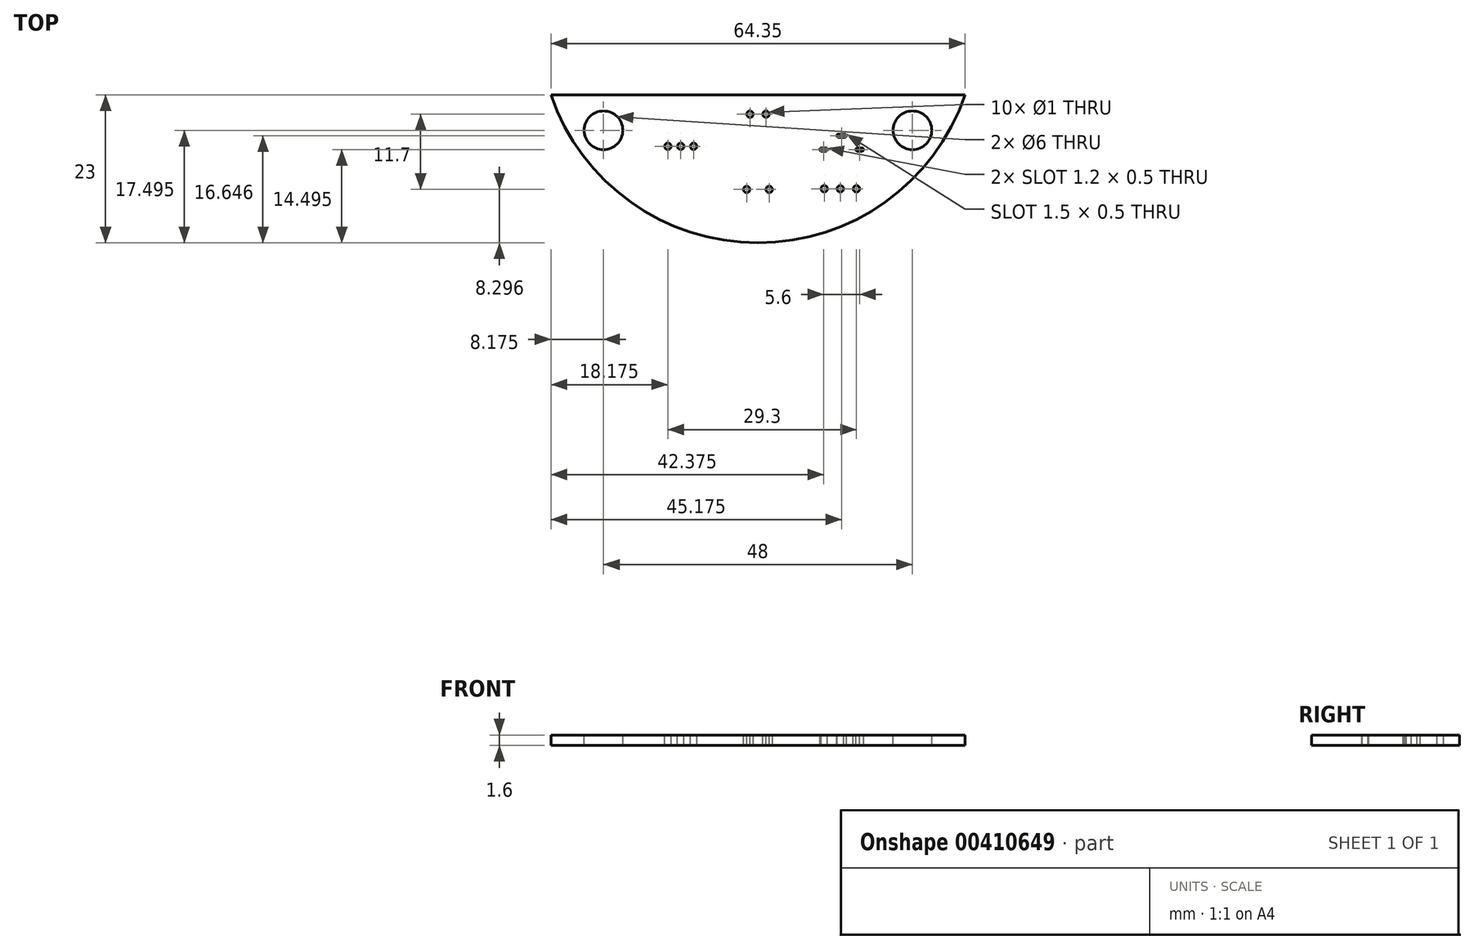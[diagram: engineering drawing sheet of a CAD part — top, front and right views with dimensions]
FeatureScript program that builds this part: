
annotation { "Feature Type Name" : "Feature", "Feature Type Description" : "" }
export const myFeature = defineFeature(function(context is Context, id is Id, definition is map)
    precondition{}
    {
        {
            var Q0;
            Q0=qCreatedBy(makeId("Top.planeOp"),FACE);
            var sketch = newSketch(context, id + "F0", { "sketchPlane" : qUnion([Q0])});
            skLineSegment(sketch, "E0.bottom", {"start": v(6.37, 29.29) * mm, "end": v(70.72, 29.29) * mm});
            skPoint(sketch, "E1.middle", {"position": v(38.54, 20.77) * mm});
            skPoint(sketch, "E2.orphan", {"position": v(18.04, 25.29) * mm});
            skPoint(sketch, "E3.orphan", {"position": v(59.04, 25.29) * mm});
            skArc(sketch, "E4", {"start": v(6.37, 29.29) * mm, "mid": v(38.54, 6.29) * mm, "end": v(70.72, 29.29) * mm});
            skSolve(sketch);
        }
        {
            var Q0;
            Q0=qSketchRegion(id+"F0",true);
            extrude(context, id + "F1", {"entities" : qUnion([Q0]), "depth" : 1.6 * mm});
        }
        {
            var Q0;
            Q0=makeQuery(id+"F1.opExtrude","CAP_FACE",FACE,{"disambiguationData":[OSD([sQuery(id+"F0.wireOp",EDGE,"E0.bottom"),sQuery(id+"F0.wireOp",EDGE,"E0.top"),sQuery(id+"F0.wireOp",EDGE,"E0.left"),sQuery(id+"F0.wireOp",EDGE,"E0.right"),sQuery(id+"F0.wireOp",EDGE,"E1.bottom"),sQuery(id+"F0.wireOp",EDGE,"E1.left"),sQuery(id+"F0.wireOp",EDGE,"E1.right")])],"isStart":false});
            var sketch = newSketch(context, id + "F2", { "sketchPlane" : qUnion([Q0])});
            skCircle(sketch, "E5", {"center": v(14.54, 23.79) * mm, "radius": 3 * mm});
            skLineSegment(sketch, "E6", {"start": v(38.54, 20.12) * mm, "end": v(38.54, 29.29) * mm, "construction": true});
            skCircle(sketch, "E7.MirrorC", {"center": v(62.54, 23.79) * mm, "radius": 3 * mm});
            skSolve(sketch);
        }
        {
            var Q0;
            Q0=qSketchRegion(id+"F2",true);
            extrude(context, id + "F3", {"entities" : qUnion([Q0]), "operationType" : NewBodyOperationType.REMOVE, "oppositeDirection" : true, "depth" : 3 * mm});
        }
        {
            var Q0;
            Q0=makeQuery(id+"F1.opExtrude","CAP_FACE",FACE,{"disambiguationData":[OSD([sQuery(id+"F0.wireOp",EDGE,"E0.bottom"),sQuery(id+"F0.wireOp",EDGE,"E0.top"),sQuery(id+"F0.wireOp",EDGE,"E0.left"),sQuery(id+"F0.wireOp",EDGE,"E0.right"),sQuery(id+"F0.wireOp",EDGE,"E1.bottom"),sQuery(id+"F0.wireOp",EDGE,"E1.left"),sQuery(id+"F0.wireOp",EDGE,"E1.right")])],"isStart":false});
            var sketch = newSketch(context, id + "F4", { "sketchPlane" : qUnion([Q0])});
            skCircle(sketch, "E8", {"center": v(24.54, 21.29) * mm, "radius": 0.5 * mm});
            skLineSegment(sketch, "E9", {"start": v(38.54, 22.32) * mm, "end": v(38.54, 29.29) * mm, "construction": true});
            skCircle(sketch, "E10.1.0.0", {"center": v(26.54, 21.29) * mm, "radius": 0.5 * mm});
            skLineSegment(sketch, "E10.direction1", {"start": v(24.54, 21.29) * mm, "end": v(26.54, 21.29) * mm, "construction": true});
            skCircle(sketch, "E11.0.2.0", {"center": v(28.54, 21.29) * mm, "radius": 0.5 * mm});
            skSolve(sketch);
        }
        {
            var Q0;
            Q0=makeQuery(id+"F1.opExtrude","CAP_FACE",FACE,{"disambiguationData":[OSD([sQuery(id+"F0.wireOp",EDGE,"E0.bottom"),sQuery(id+"F0.wireOp",EDGE,"E4")])],"isStart":false});
            var sketch = newSketch(context, id + "F5", { "sketchPlane" : qUnion([Q0])});
            skLineSegment(sketch, "E12", {"start": v(51.54, 14.1) * mm, "end": v(51.54, 27.42) * mm, "construction": true});
            skLineSegment(sketch, "E13", {"start": v(38.54, 6.29) * mm, "end": v(38.54, 24.04) * mm, "construction": true});
            skLineSegment(sketch, "E14", {"start": v(48.4, 20.79) * mm, "end": v(49.1, 20.79) * mm, "construction": true});
            skLineSegment(sketch, "E15", {"start": v(48.74, 20.79) * mm, "end": v(48.74, 23.97) * mm, "construction": true});
            skLineSegment(sketch, "E16", {"start": v(51.04, 22.94) * mm, "end": v(52.04, 22.94) * mm, "construction": true});
            skLineSegment(sketch, "E17", {"start": v(51.54, 22.94) * mm, "end": v(51.54, 19.92) * mm, "construction": true});
            skArc(sketch, "E18.0.startCap", {"start": v(51.04, 22.69) * mm, "mid": v(50.8, 22.94) * mm, "end": v(51.04, 23.19) * mm});
            skArc(sketch, "E18.0.endCap", {"start": v(52.04, 23.19) * mm, "mid": v(52.3, 22.94) * mm, "end": v(52.04, 22.69) * mm});
            skLineSegment(sketch, "E18.0.left", {"start": v(51.04, 23.19) * mm, "end": v(52.04, 23.19) * mm});
            skLineSegment(sketch, "E18.0.right", {"start": v(51.04, 22.69) * mm, "end": v(52.04, 22.69) * mm});
            skLineSegment(sketch, "E19", {"start": v(50.45, 21.94) * mm, "end": v(53.65, 21.94) * mm, "construction": true});
            skArc(sketch, "E20.0.startCap", {"start": v(49.1, 21.04) * mm, "mid": v(49.34, 20.79) * mm, "end": v(49.1, 20.54) * mm});
            skArc(sketch, "E20.0.endCap", {"start": v(48.4, 20.54) * mm, "mid": v(48.14, 20.79) * mm, "end": v(48.4, 21.04) * mm});
            skLineSegment(sketch, "E20.0.left", {"start": v(48.4, 20.54) * mm, "end": v(49.1, 20.54) * mm});
            skLineSegment(sketch, "E20.0.right", {"start": v(48.4, 21.04) * mm, "end": v(49.1, 21.04) * mm});
            skArc(sketch, "E21.MirrorCS", {"start": v(54.7, 20.54) * mm, "mid": v(54.94, 20.79) * mm, "end": v(54.7, 21.04) * mm});
            skLineSegment(sketch, "E22.MirrorCS", {"start": v(54.7, 20.54) * mm, "end": v(54, 20.54) * mm});
            skLineSegment(sketch, "E23.MirrorCS", {"start": v(54.7, 21.04) * mm, "end": v(54, 21.04) * mm});
            skArc(sketch, "E24.MirrorCS", {"start": v(54, 21.04) * mm, "mid": v(53.74, 20.79) * mm, "end": v(54, 20.54) * mm});
            skSolve(sketch);
        }
        {
            var Q0;
            Q0=makeQuery(id+"F1.opExtrude","CAP_FACE",FACE,{"disambiguationData":[OSD([sQuery(id+"F0.wireOp",EDGE,"E0.bottom"),sQuery(id+"F0.wireOp",EDGE,"E4")])],"isStart":false});
            var sketch = newSketch(context, id + "F6", { "sketchPlane" : qUnion([Q0])});
            skCircle(sketch, "E25", {"center": v(48.84, 14.69) * mm, "radius": 0.5 * mm});
            skCircle(sketch, "E26.1.0.0", {"center": v(53.84, 14.69) * mm, "radius": 0.5 * mm});
            skLineSegment(sketch, "E26.direction1", {"start": v(48.84, 14.69) * mm, "end": v(53.84, 14.69) * mm, "construction": true});
            skLineSegment(sketch, "E27", {"start": v(38.54, 6.29) * mm, "end": v(38.54, 17.65) * mm, "construction": true});
            skLineSegment(sketch, "E28", {"start": v(51.34, 14.69) * mm, "end": v(51.34, 23.7) * mm, "construction": true});
            skCircle(sketch, "E29", {"center": v(51.34, 14.69) * mm, "radius": 0.5 * mm});
            skSolve(sketch);
        }
        {
            var Q0;
            Q0=makeQuery(id+"F1.opExtrude","CAP_FACE",FACE,{"disambiguationData":[OSD([sQuery(id+"F0.wireOp",EDGE,"E0.bottom"),sQuery(id+"F0.wireOp",EDGE,"E4")])],"isStart":false});
            var sketch = newSketch(context, id + "F7", { "sketchPlane" : qUnion([Q0])});
            skCircle(sketch, "E30", {"center": v(37.3, 26.29) * mm, "radius": 0.5 * mm});
            skCircle(sketch, "E31.1.0.0", {"center": v(39.8, 26.29) * mm, "radius": 0.5 * mm});
            skLineSegment(sketch, "E31.direction1", {"start": v(37.3, 26.29) * mm, "end": v(39.8, 26.29) * mm, "construction": true});
            skLineSegment(sketch, "E32", {"start": v(38.54, 15.29) * mm, "end": v(38.54, 29.29) * mm, "construction": true});
            skLineSegment(sketch, "E33", {"start": v(38.54, 26.14) * mm, "end": v(38.54, 26.29) * mm, "construction": true});
            skSolve(sketch);
        }
        {
            var Q0;
            Q0=makeQuery(id+"F1.opExtrude","CAP_FACE",FACE,{"disambiguationData":[OSD([sQuery(id+"F0.wireOp",EDGE,"E0.bottom"),sQuery(id+"F0.wireOp",EDGE,"E4")])],"isStart":false});
            var sketch = newSketch(context, id + "F8", { "sketchPlane" : qUnion([Q0])});
            skCircle(sketch, "E34", {"center": v(36.8, 14.59) * mm, "radius": 0.5 * mm});
            skCircle(sketch, "E35.1.0.0", {"center": v(40.3, 14.59) * mm, "radius": 0.5 * mm});
            skLineSegment(sketch, "E35.direction1", {"start": v(36.8, 14.59) * mm, "end": v(40.3, 14.59) * mm, "construction": true});
            skLineSegment(sketch, "E36", {"start": v(38.54, 25.9) * mm, "end": v(38.54, 14.59) * mm, "construction": true});
            skSolve(sketch);
        }
        {
            var Q0;
            Q0=qSketchRegion(id+"F6",true);
            var Q1;
            Q1=qSketchRegion(id+"F7",true);
            var Q2;
            Q2=qSketchRegion(id+"F8",true);
            var Q3;
            Q3=qSketchRegion(id+"F5",true);
            var Q4;
            Q4=qSketchRegion(id+"F4",true);
            extrude(context, id + "F9", {"entities" : qUnion([Q0, Q1, Q2, Q3, Q4]), "operationType" : NewBodyOperationType.REMOVE, "oppositeDirection" : true, "depth" : 4 * mm});
        }
        {
            var Q0;
            Q0=makeQuery(id+"F1.opExtrude","CAP_FACE",FACE,{"disambiguationData":[OSD([sQuery(id+"F0.wireOp",EDGE,"E0.bottom"),sQuery(id+"F0.wireOp",EDGE,"E4")])],"isStart":true});
            var sketch = newSketch(context, id + "F10", { "sketchPlane" : qUnion([Q0])});
            skCircle(sketch, "E37", {"center": v(62.54, -23.79) * mm, "radius": 2.1 * mm});
            skLineSegment(sketch, "E38", {"start": v(38.54, -29.29) * mm, "end": v(38.54, 3.6) * mm, "construction": true});
            skCircle(sketch, "E39.MirrorC", {"center": v(14.54, -23.79) * mm, "radius": 2.1 * mm});
            skSolve(sketch);
        }
        {
            var Q0;
            Q0=qSketchRegion(id+"F10",true);
            extrude(context, id + "F11", {"entities" : qUnion([Q0]), "operationType" : NewBodyOperationType.REMOVE, "oppositeDirection" : true, "depth" : .2 * mm});
        }
    });
